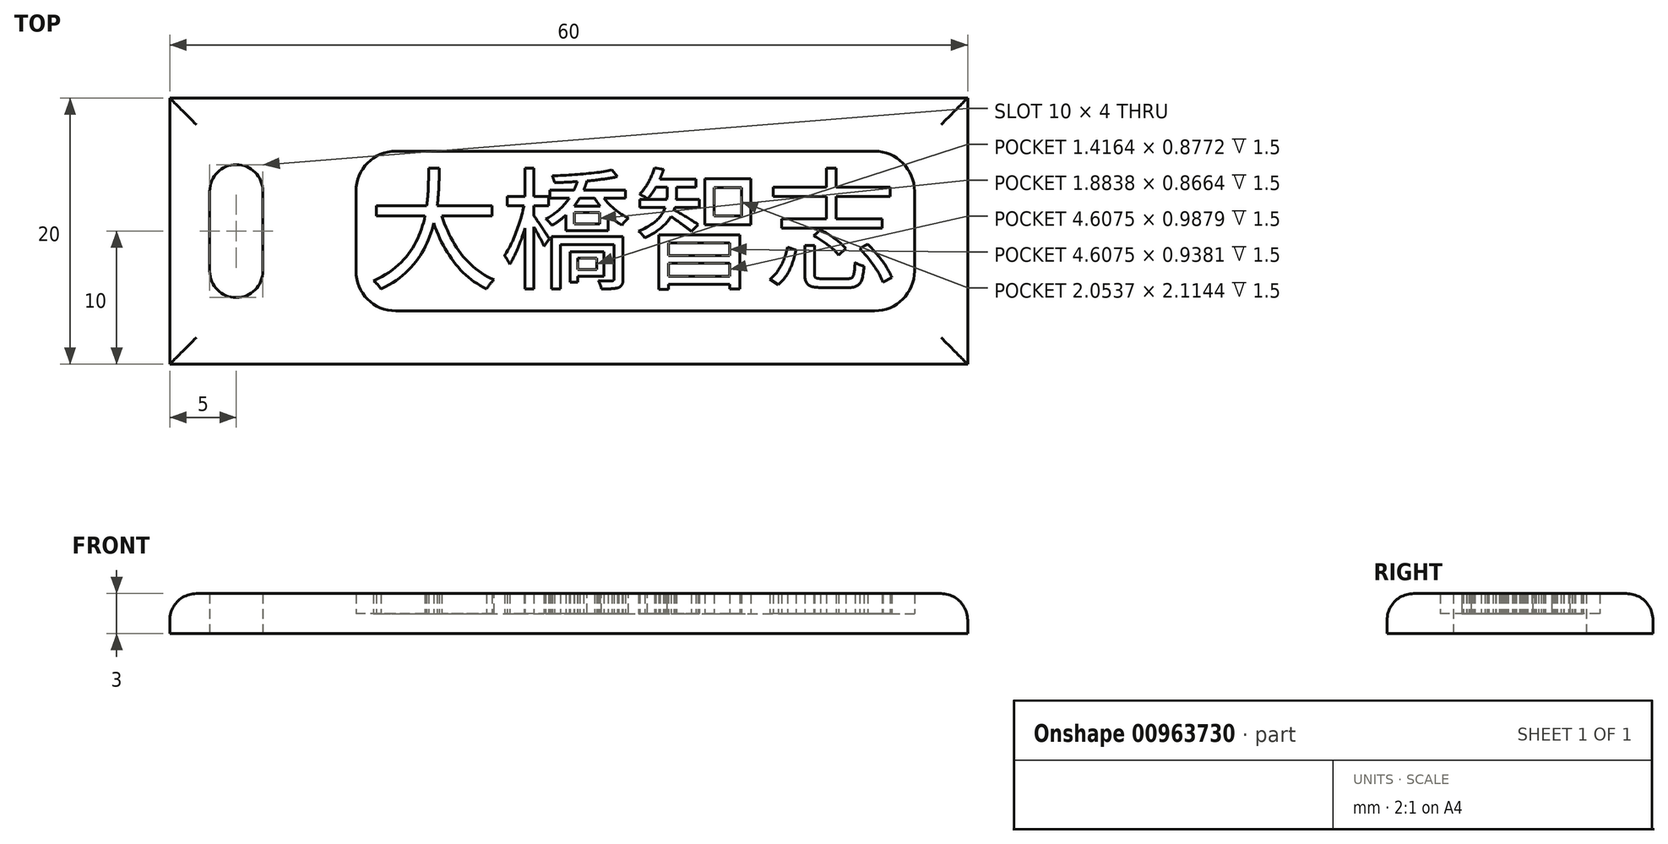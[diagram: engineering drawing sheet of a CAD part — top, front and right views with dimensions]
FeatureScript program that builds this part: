
annotation { "Feature Type Name" : "Feature", "Feature Type Description" : "" }
export const myFeature = defineFeature(function(context is Context, id is Id, definition is map)
    precondition{}
    {
        {
            var Q0;
            Q0=qCreatedBy(makeId("Top.planeOp"),FACE);
            var sketch = newSketch(context, id + "F0", { "sketchPlane" : qUnion([Q0])});
            skLineSegment(sketch, "E0.bottom", {"start": v(25, 10) * mm, "end": v(-25, 10) * mm});
            skLineSegment(sketch, "E0.top", {"start": v(25, -10) * mm, "end": v(-25, -10) * mm});
            skLineSegment(sketch, "E0.left", {"start": v(25, 10) * mm, "end": v(25, -10) * mm});
            skLineSegment(sketch, "E0.right", {"start": v(-25, 10) * mm, "end": v(-25, -10) * mm});
            skPoint(sketch, "E0.middle", {"position": v(0, 0) * mm});
            skLineSegment(sketch, "E1.bottom", {"start": v(-25, 10) * mm, "end": v(-35, 10) * mm});
            skLineSegment(sketch, "E1.top", {"start": v(-25, -10) * mm, "end": v(-35, -10) * mm});
            skLineSegment(sketch, "E1.right", {"start": v(-35, 10) * mm, "end": v(-35, -10) * mm});
            skPoint(sketch, "E1.middle", {"position": v(-30, 0) * mm});
            skLineSegment(sketch, "E2.bottom", {"start": v(-30, 5) * mm, "end": v(-30, 5) * mm});
            skLineSegment(sketch, "E2.top", {"start": v(-30, -5) * mm, "end": v(-30, -5) * mm});
            skLineSegment(sketch, "E2.left", {"start": v(-28, 3) * mm, "end": v(-28, -3) * mm});
            skLineSegment(sketch, "E2.right", {"start": v(-32, 3) * mm, "end": v(-32, -3) * mm});
            skPoint(sketch, "E3.visualSharp", {"position": v(-32, 5) * mm});
            skArc(sketch, "E3.filletArc", {"start": v(-30, 5) * mm, "mid": v(-31.41, 4.41) * mm, "end": v(-32, 3) * mm});
            skPoint(sketch, "E4.visualSharp", {"position": v(-28, 5) * mm});
            skArc(sketch, "E4.filletArc", {"start": v(-28, 3) * mm, "mid": v(-28.59, 4.41) * mm, "end": v(-30, 5) * mm});
            skPoint(sketch, "E5.visualSharp", {"position": v(-32, -5) * mm});
            skArc(sketch, "E5.filletArc", {"start": v(-32, -3) * mm, "mid": v(-31.41, -4.41) * mm, "end": v(-30, -5) * mm});
            skPoint(sketch, "E6.visualSharp", {"position": v(-28, -5) * mm});
            skArc(sketch, "E6.filletArc", {"start": v(-30, -5) * mm, "mid": v(-28.59, -4.41) * mm, "end": v(-28, -3) * mm});
            skSolve(sketch);
        }
        {
            var Q0;
            Q0 = qSketchRegion(id + "F0", true);
            extrude(context, id + "F1", {"entities" : qUnion([Q0]), "depth" : 3 * mm, "offsetDistance" : 25 * mm});
        }
        {
            var Q0;
            Q0=qCreatedBy(makeId("Top.planeOp"),FACE);
            var sketch = newSketch(context, id + "F2", { "sketchPlane" : qUnion([Q0])});
            skLineSegment(sketch, "E7.bottom", {"start": v(-18, 6) * mm, "end": v(18, 6) * mm});
            skLineSegment(sketch, "E7.top", {"start": v(-18, -6) * mm, "end": v(18, -6) * mm});
            skLineSegment(sketch, "E7.left", {"start": v(-21, 3) * mm, "end": v(-21, -3) * mm});
            skLineSegment(sketch, "E7.right", {"start": v(21, 3) * mm, "end": v(21, -3) * mm});
            skPoint(sketch, "E7.middle", {"position": v(0, 0) * mm});
            skPoint(sketch, "E8.visualSharp", {"position": v(-21, 6) * mm});
            skArc(sketch, "E8.filletArc", {"start": v(-18, 6) * mm, "mid": v(-20.12, 5.12) * mm, "end": v(-21, 3) * mm});
            skPoint(sketch, "E9.visualSharp", {"position": v(-21, -6) * mm});
            skArc(sketch, "E9.filletArc", {"start": v(-21, -3) * mm, "mid": v(-20.12, -5.12) * mm, "end": v(-18, -6) * mm});
            skPoint(sketch, "E10.visualSharp", {"position": v(21, 6) * mm});
            skArc(sketch, "E10.filletArc", {"start": v(21, 3) * mm, "mid": v(20.12, 5.12) * mm, "end": v(18, 6) * mm});
            skPoint(sketch, "E11.visualSharp", {"position": v(21, -6) * mm});
            skArc(sketch, "E11.filletArc", {"start": v(18, -6) * mm, "mid": v(20.12, -5.12) * mm, "end": v(21, -3) * mm});
            skSolve(sketch);
        }
        {
            var Q0;
            Q0 = qSketchRegion(id + "F2", true);
            extrude(context, id + "F3", {"entities" : qUnion([Q0]), "depth" : 3 * mm, "offsetDistance" : 25 * mm});
        }
        {
            var Q0;
            Q0=makeQuery(id+"F3.opExtrude","SWEPT_BODY",BODY,{"disambiguationData":[OSD([sQuery(id+"F2.wireOp",EDGE,"E7.bottom"),sQuery(id+"F2.wireOp",EDGE,"E7.top"),sQuery(id+"F2.wireOp",EDGE,"E7.left"),sQuery(id+"F2.wireOp",EDGE,"E7.right"),sQuery(id+"F2.wireOp",EDGE,"E8.filletArc"),sQuery(id+"F2.wireOp",EDGE,"E9.filletArc"),sQuery(id+"F2.wireOp",EDGE,"E10.filletArc"),sQuery(id+"F2.wireOp",EDGE,"E11.filletArc")])]});
            transform(context, id + "F4", {"entities" : qUnion([Q0]), "transformType" : TransformType.TRANSLATION_3D, "dx" : 0 * mm, "dy" : 0 * mm, "dz" : 1.5 * mm, "makeCopy" : false});
        }
        {
            var Q0;
            Q0=makeQuery(id+"F3.opExtrude","SWEPT_BODY",BODY,{"disambiguationData":[OSD([sQuery(id+"F2.wireOp",EDGE,"E7.bottom"),sQuery(id+"F2.wireOp",EDGE,"E7.top"),sQuery(id+"F2.wireOp",EDGE,"E7.left"),sQuery(id+"F2.wireOp",EDGE,"E7.right"),sQuery(id+"F2.wireOp",EDGE,"E8.filletArc"),sQuery(id+"F2.wireOp",EDGE,"E9.filletArc"),sQuery(id+"F2.wireOp",EDGE,"E10.filletArc"),sQuery(id+"F2.wireOp",EDGE,"E11.filletArc")])]});
            var Q1;
            Q1=makeQuery(id+"F1.opExtrude","SWEPT_BODY",BODY,{"disambiguationData":[OSD([sQuery(id+"F0.wireOp",EDGE,"E0.bottom"),sQuery(id+"F0.wireOp",EDGE,"E0.top"),sQuery(id+"F0.wireOp",EDGE,"E0.left"),sQuery(id+"F0.wireOp",EDGE,"E1.bottom"),sQuery(id+"F0.wireOp",EDGE,"E1.top"),sQuery(id+"F0.wireOp",EDGE,"E1.right"),sQuery(id+"F0.wireOp",EDGE,"E2.left"),sQuery(id+"F0.wireOp",EDGE,"E2.right"),sQuery(id+"F0.wireOp",EDGE,"E3.filletArc"),sQuery(id+"F0.wireOp",EDGE,"E4.filletArc"),sQuery(id+"F0.wireOp",EDGE,"E5.filletArc"),sQuery(id+"F0.wireOp",EDGE,"E6.filletArc")])]});
            booleanBodies(context, id + "F5", {"operationType" : BooleanOperationType.SUBTRACTION, "tools" : qUnion([Q0]), "targets" : qUnion([Q1])});
        }
        {
            var Q0;
            Q0=qCreatedBy(makeId("Top.planeOp"),FACE);
            var sketch = newSketch(context, id + "F6", { "sketchPlane" : qUnion([Q0])});
            skText(sketch, "E12", { "text": "大橋智志", "fontName": "NotoSansCJKjp-Regular.otf"});
            const initialGuessF6  = {"E12": [-0.02014, -0.0036, 1, 0, 0.00718]};
            skSetInitialGuess(sketch, initialGuessF6);
            skSolve(sketch);
        }
        {
            var Q0;
            Q0 = qSketchRegion(id + "F6", true);
            extrude(context, id + "F7", {"entities" : qUnion([Q0]), "operationType" : NewBodyOperationType.ADD, "depth" : 3 * mm, "offsetDistance" : 25 * mm});
        }
        {
            var Q0;
            Q0=makeQuery(id+"F1.opExtrude","CAP_EDGE",EDGE,{"disambiguationData":[OSD([sQuery(id+"F0.wireOp",EDGE,"E0.bottom"),sQuery(id+"F0.wireOp",EDGE,"E1.bottom")])],"isStart":false});
            var Q1;
            Q1=makeQuery(id+"F1.opExtrude","CAP_EDGE",EDGE,{"disambiguationData":[OSD([sQuery(id+"F0.wireOp",EDGE,"E1.right")])],"isStart":false});
            var Q2;
            Q2=makeQuery(id+"F1.opExtrude","CAP_EDGE",EDGE,{"disambiguationData":[OSD([sQuery(id+"F0.wireOp",EDGE,"E0.top"),sQuery(id+"F0.wireOp",EDGE,"E1.top")])],"isStart":false});
            var Q3;
            Q3=makeQuery(id+"F1.opExtrude","CAP_EDGE",EDGE,{"disambiguationData":[OSD([sQuery(id+"F0.wireOp",EDGE,"E0.left")])],"isStart":false});
            fillet(context, id + "F8", {"entities" : qUnion([Q0, Q1, Q2, Q3]), "radius" : 2 * mm, "tangentPropagation" : true, "allowEdgeOverflow" : false});
        }
    });
